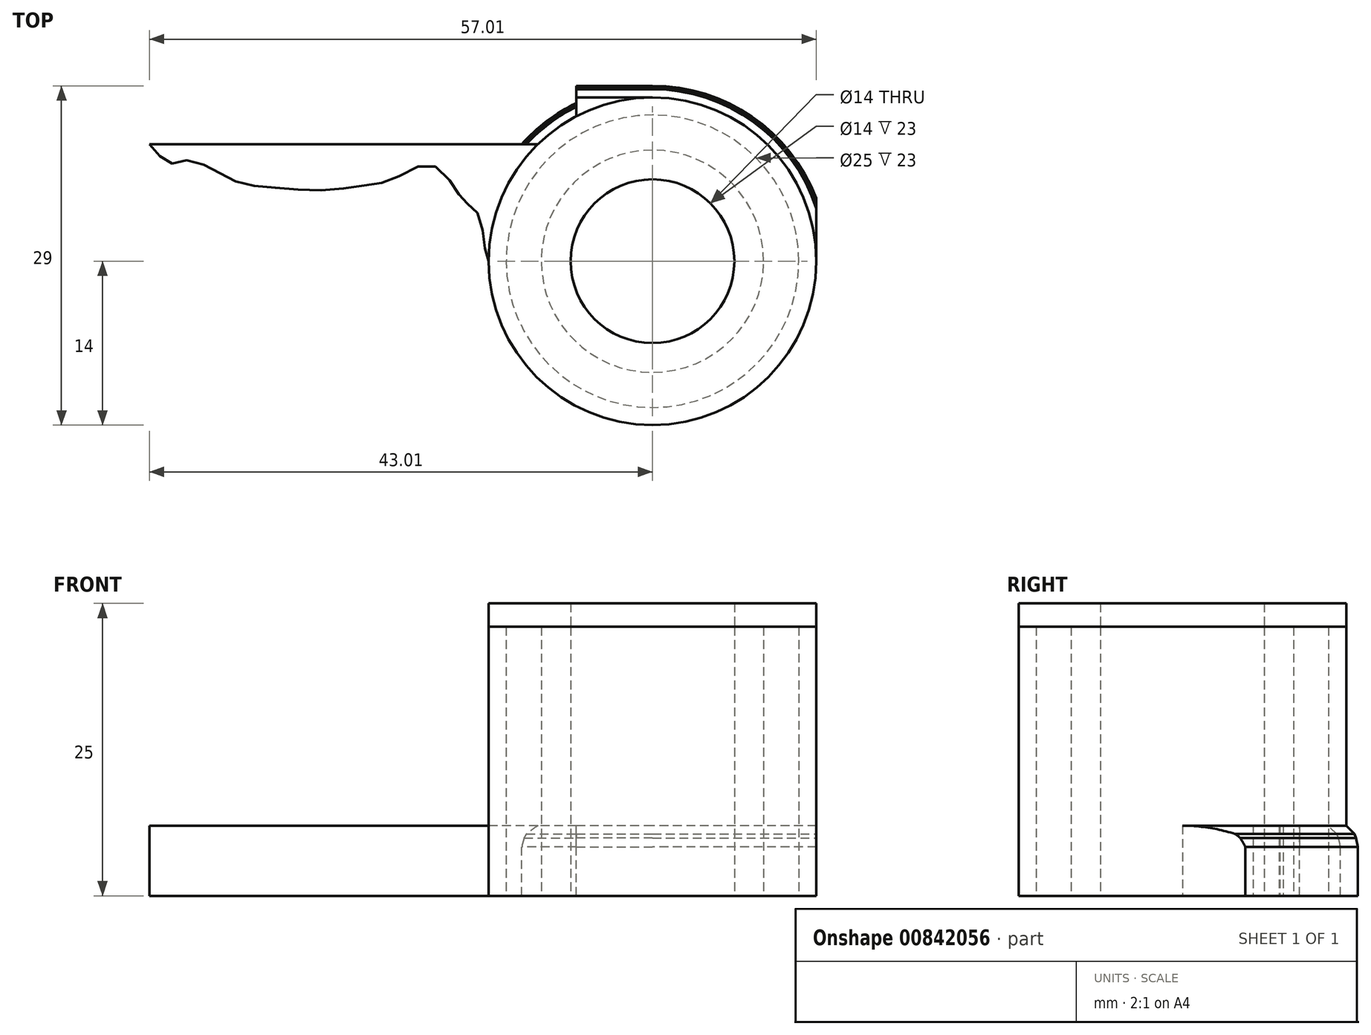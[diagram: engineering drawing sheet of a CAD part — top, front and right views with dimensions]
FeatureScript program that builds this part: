
annotation { "Feature Type Name" : "Feature", "Feature Type Description" : "" }
export const myFeature = defineFeature(function(context is Context, id is Id, definition is map)
    precondition{}
    {
        {
            var Q0;
            Q0=qCreatedBy(makeId("Top.planeOp"),FACE);
            var sketch = newSketch(context, id + "F0", { "sketchPlane" : qUnion([Q0])});
            skCircle(sketch, "E0", {"center": v(0, 0) * mm, "radius": 7 * mm});
            skCircle(sketch, "E1", {"center": v(0, 0) * mm, "radius": 9.5 * mm});
            skCircle(sketch, "E2", {"center": v(0, 0) * mm, "radius": 12.5 * mm});
            skCircle(sketch, "E3", {"center": v(0, 0) * mm, "radius": 14 * mm});
            skArc(sketch, "E4", {"start": v(15, 0) * mm, "mid": v(0, 15) * mm, "end": v(-15, 0) * mm});
            skLineSegment(sketch, "E5", {"start": v(-14, 0) * mm, "end": v(-14, 7.91) * mm});
            skLineSegment(sketch, "E6", {"start": v(14, 0) * mm, "end": v(14, 12.1) * mm});
            skSolve(sketch);
        }
        {
            var Q0;
            Q0=makeQuery(id+"F0.imprint","IMPRINT",FACE,{"disambiguationData":[TD([[makeQuery(id+"F0.imprint","IMPRINT",EDGE,{"derivedFrom":sQuery(id+"F0.wireOp",EDGE,"E2")}),-1.0]])]});
            var Q1;
            Q1=makeQuery(id+"F0.imprint","IMPRINT",FACE,{"disambiguationData":[TD([[makeQuery(id+"F0.imprint","IMPRINT",EDGE,{"derivedFrom":sQuery(id+"F0.wireOp",EDGE,"E0")}),-1.0]])]});
            extrude(context, id + "F1", {"entities" : qUnion([Q0, Q1]), "depth" : 23 * mm, "offsetDistance" : 25 * mm});
        }
        {
            var Q0;
            {var subQ0=sQuery(id+"F0.wireOp",EDGE,"E5");var subQ1=sQuery(id+"F0.wireOp",EDGE,"E3");var subQ2=makeQuery(id+"F0.imprint","INTERSECT",VERTEX,{"derivedFrom":[subQ1,subQ0]});Q0=makeQuery(id+"F0.imprint","IMPRINT",FACE,{"disambiguationData":[TD([[makeQuery(id+"F0.imprint","IMPRINT",EDGE,{"disambiguationData":[TD([[subQ2,1.0]])],"derivedFrom":subQ1}),-1.0]])]});}
            extrude(context, id + "F2", {"entities" : qUnion([Q0]), "operationType" : NewBodyOperationType.ADD, "depth" : 6 * mm, "offsetDistance" : 25 * mm});
        }
        {
            var Q0;
            Q0=makeQuery(id+"F1.opExtrude","CAP_FACE",FACE,{"disambiguationData":[OSD([sQuery(id+"F0.wireOp",EDGE,"E2"),sQuery(id+"F0.wireOp",EDGE,"E3")])],"isStart":false});
            var sketch = newSketch(context, id + "F3", { "sketchPlane" : qUnion([Q0])});
            skCircle(sketch, "E7", {"center": v(0, 0) * mm, "radius": 14 * mm});
            skCircle(sketch, "E8", {"center": v(0, 0) * mm, "radius": 7 * mm});
            skSolve(sketch);
        }
        {
            var Q0;
            Q0 = qSketchRegion(id + "F3", true);
            extrude(context, id + "F4", {"entities" : qUnion([Q0]), "depth" : 2 * mm, "offsetDistance" : 25 * mm});
        }
        {
            var Q0;
            Q0=makeQuery(id+"F2.opExtrude","CAP_FACE",FACE,{"disambiguationData":[OSD([sQuery(id+"F0.wireOp",EDGE,"E3"),sQuery(id+"F0.wireOp",EDGE,"E4"),sQuery(id+"F0.wireOp",EDGE,"E5"),sQuery(id+"F0.wireOp",EDGE,"E6")])],"isStart":false});
            var sketch = newSketch(context, id + "F5", { "sketchPlane" : qUnion([Q0])});
            skLineSegment(sketch, "E9.bottom", {"start": v(0, 15) * mm, "end": v(-49, 15) * mm});
            skLineSegment(sketch, "E9.top", {"start": v(0, 10) * mm, "end": v(-49, 10) * mm});
            skLineSegment(sketch, "E9.left", {"start": v(0, 15) * mm, "end": v(0, 10) * mm});
            skLineSegment(sketch, "E9.right", {"start": v(-49, 15) * mm, "end": v(-49, 10) * mm});
            skLineSegment(sketch, "E10.bottom", {"start": v(-49, 15) * mm, "end": v(-6.5, 15) * mm});
            skLineSegment(sketch, "E10.top", {"start": v(-49, 10) * mm, "end": v(-6.5, 10) * mm});
            skLineSegment(sketch, "E10.right", {"start": v(-6.5, 15) * mm, "end": v(-6.5, 10) * mm});
            skFitSpline(sketch, "E11", {"points": [v(-49, 15) * mm, v(-49, 10) * mm, v(-46.63, 3.53) * mm, v(-44.81, 4.75) * mm, v(-44.11, 7.5) * mm, v(-43, 10) * mm, v(-41.56, 8.44) * mm, v(-40.06, 8.6) * mm, v(-37.73, 7.94) * mm, v(-35.46, 6.77) * mm, v(-32.24, 6.27) * mm, v(-28.08, 6.07) * mm, v(-24.44, 6.5) * mm, v(-21.94, 7.1) * mm, v(-19.04, 8.26) * mm, v(-16.98, 6.38) * mm, v(-16.06, 5.12) * mm, v(-14.99, 4.16) * mm, v(-14.38, 1.56) * mm, v(-14, 0) * mm], "startDerivative": vector(19.5, -64.67) * mm, "endDerivative": vector(17.7, -33.1) * mm});
            skSolve(sketch);
        }
        {
            var Q0;
            {var subQ5=makeQuery(id+"F2.opExtrude","CAP_EDGE",EDGE,{"disambiguationData":[OSD([sQuery(id+"F0.wireOp",EDGE,"E5")])],"isStart":false});Q0=makeQuery(id+"F5.imprint","IMPRINT",FACE,{"disambiguationData":[TD([[makeQuery(id+"F5.imprint","IMPRINT",EDGE,{"derivedFrom":subQ5}),1.0]])]});}
            var Q1;
            {var subQ0=sQuery(id+"F5.wireOp",EDGE,"E11");var subQ1=sQuery(id+"F5.wireOp",EDGE,"E10.top");var subQ3=makeQuery(id+"F5.imprint","INTERSECT",VERTEX,{"disambiguationData":[OD(0.0)],"derivedFrom":[subQ1,subQ0]});Q1=makeQuery(id+"F5.imprint","IMPRINT",FACE,{"disambiguationData":[TD([[makeQuery(id+"F5.imprint","IMPRINT",EDGE,{"disambiguationData":[TD([[subQ3,1.0]])],"derivedFrom":subQ1}),-1.0]])]});}
            var Q2;
            {var subQ9=sQuery(id+"F5.wireOp",EDGE,"E10.bottom");Q2=makeQuery(id+"F5.imprint","IMPRINT",FACE,{"disambiguationData":[TD([[makeQuery(id+"F5.imprint","IMPRINT",EDGE,{"derivedFrom":subQ9}),-1.0]])]});}
            var Q3;
            {var subQ0=sQuery(id+"F5.wireOp",EDGE,"E9.bottom");Q3=makeQuery(id+"F5.imprint","IMPRINT",FACE,{"disambiguationData":[TD([[makeQuery(id+"F5.imprint","IMPRINT",EDGE,{"derivedFrom":subQ0}),1.0]])]});}
            extrude(context, id + "F6", {"entities" : qUnion([Q0, Q1, Q2, Q3]), "operationType" : NewBodyOperationType.ADD, "oppositeDirection" : true, "depth" : 6 * mm, "offsetDistance" : 25 * mm});
        }
        {
            var Q0;
            Q0=makeQuery(id+"F2.opExtrude","CAP_EDGE",EDGE,{"disambiguationData":[OSD([sQuery(id+"F0.wireOp",EDGE,"E4")])],"isStart":false});
            chamfer(context, id + "F7", {"entities" : qUnion([Q0]), "width" : 1 * mm, "tangentPropagation" : true});
        }
        {
            var Q0;
            {var subQ0=sQuery(id+"F0.wireOp",EDGE,"E4");Q0=makeQuery(id+"F7.opChamfer","BLEND_EDGE",EDGE,{"blendedFrom":[makeQuery(id+"F2.opExtrude","CAP_EDGE",EDGE,{"disambiguationData":[OSD([subQ0])],"isStart":false}),makeQuery(id+"F2.opExtrude","SWEPT_FACE",FACE,{"disambiguationData":[OSD([subQ0])]})],"blendedInto":[makeQuery(id+"F2.opExtrude","SWEPT_FACE",FACE,{"disambiguationData":[OSD([subQ0])]})]});}
            chamfer(context, id + "F8", {"entities" : qUnion([Q0]), "width" : 1 * mm, "tangentPropagation" : true});
        }
        {
            var Q0;
            {var subQ0=sQuery(id+"F0.wireOp",EDGE,"E4");var subQ1=makeQuery(id+"F2.opExtrude","SWEPT_FACE",FACE,{"disambiguationData":[OSD([subQ0])]});Q0=makeQuery(id+"F8.opChamfer","BLEND_EDGE",EDGE,{"blendedFrom":[makeQuery(id+"F7.opChamfer","BLEND_EDGE",EDGE,{"blendedFrom":[makeQuery(id+"F2.opExtrude","CAP_EDGE",EDGE,{"disambiguationData":[OSD([subQ0])],"isStart":false}),subQ1],"blendedInto":[subQ1]}),subQ1],"blendedInto":[subQ1]});}
            chamfer(context, id + "F9", {"entities" : qUnion([Q0]), "width" : 2 * mm, "tangentPropagation" : true});
        }
    });
